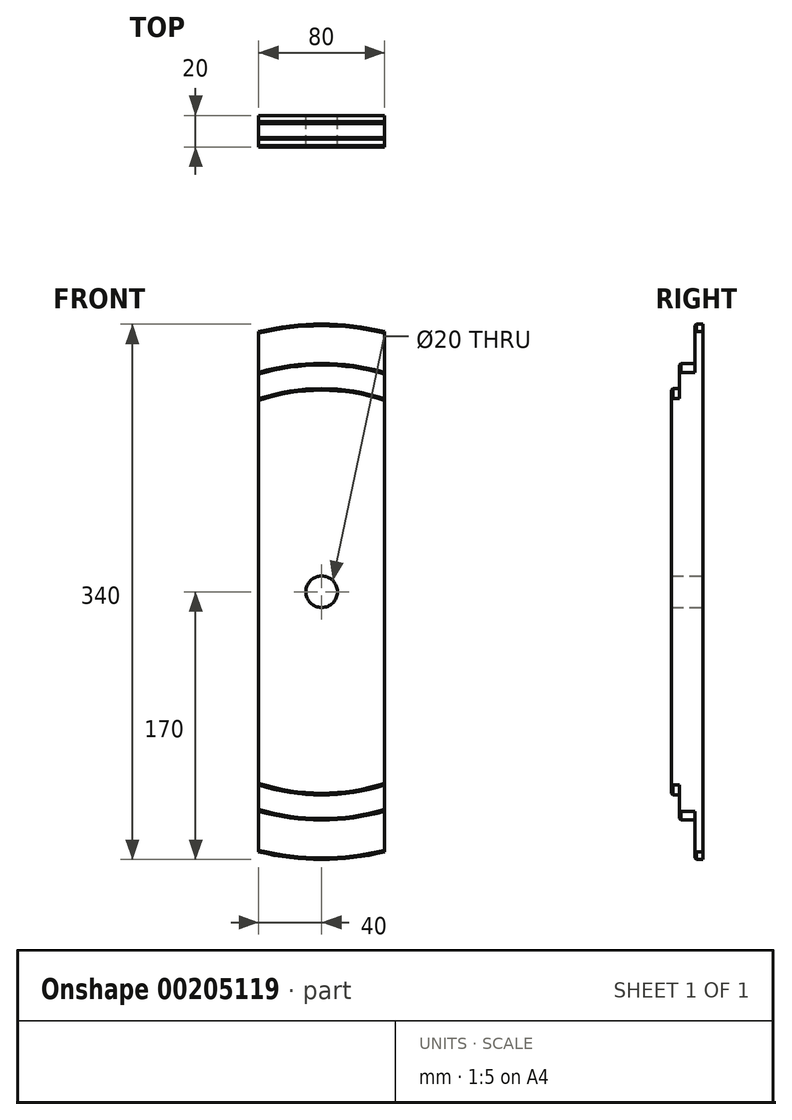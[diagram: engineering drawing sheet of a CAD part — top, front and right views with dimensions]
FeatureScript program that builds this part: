
annotation { "Feature Type Name" : "Feature", "Feature Type Description" : "" }
export const myFeature = defineFeature(function(context is Context, id is Id, definition is map)
    precondition{}
    {
        {
            var Q0;
            Q0=qCreatedBy(makeId("Front.planeOp"),FACE);
            var sketch = newSketch(context, id + "F0", { "sketchPlane" : qUnion([Q0])});
            skCircle(sketch, "E0", {"center": v(0, 0) * mm, "radius": 170 * mm});
            skCircle(sketch, "E1", {"center": v(0, 0) * mm, "radius": 145 * mm});
            skCircle(sketch, "E2", {"center": v(0, 0) * mm, "radius": 129 * mm});
            skLineSegment(sketch, "E3.bottom", {"start": v(-40, 175.47) * mm, "end": v(40, 175.47) * mm});
            skLineSegment(sketch, "E3.top", {"start": v(-40, -184.43) * mm, "end": v(40, -184.43) * mm});
            skLineSegment(sketch, "E3.left", {"start": v(-40, 175.47) * mm, "end": v(-40, -184.43) * mm});
            skLineSegment(sketch, "E3.right", {"start": v(40, 175.47) * mm, "end": v(40, -184.43) * mm});
            skCircle(sketch, "E4", {"center": v(0, 0) * mm, "radius": 10 * mm});
            skSolve(sketch);
        }
        {
            var Q0;
            Q0=makeQuery(id+"F0.imprint","IMPRINT",FACE,{"disambiguationData":[TD([[makeQuery(id+"F0.imprint","IMPRINT",EDGE,{"derivedFrom":sQuery(id+"F0.wireOp",EDGE,"E0")}),1.0]])]});
            extrude(context, id + "F1", {"entities" : qUnion([Q0]), "depth" : 5 * mm});
        }
        {
            var Q0;
            Q0=makeQuery(id+"F0.imprint","IMPRINT",FACE,{"disambiguationData":[TD([[makeQuery(id+"F0.imprint","IMPRINT",EDGE,{"derivedFrom":sQuery(id+"F0.wireOp",EDGE,"E1")}),1.0]])]});
            extrude(context, id + "F2", {"entities" : qUnion([Q0]), "operationType" : NewBodyOperationType.ADD, "depth" : 15 * mm});
        }
        {
            var Q0;
            Q0=makeQuery(id+"F0.imprint","IMPRINT",FACE,{"disambiguationData":[TD([[makeQuery(id+"F0.imprint","IMPRINT",EDGE,{"derivedFrom":sQuery(id+"F0.wireOp",EDGE,"E2")}),1.0]])]});
            extrude(context, id + "F3", {"entities" : qUnion([Q0]), "operationType" : NewBodyOperationType.ADD, "depth" : 20 * mm});
        }
        {
            var Q0;
            {var subQ0=sQuery(id+"F0.wireOp",EDGE,"E3.left");var subQ1=sQuery(id+"F0.wireOp",EDGE,"E2");var subQ2=makeQuery(id+"F0.imprint","INTERSECT",VERTEX,{"disambiguationData":[OD(0.0)],"derivedFrom":[subQ1,subQ0]});Q0=makeQuery(id+"F0.imprint","IMPRINT",FACE,{"disambiguationData":[TD([[makeQuery(id+"F0.imprint","IMPRINT",EDGE,{"disambiguationData":[TD([[subQ2,-1.0]])],"derivedFrom":subQ1}),1.0]])]});}
            var Q1;
            {var subQ0=sQuery(id+"F0.wireOp",EDGE,"E3.left");var subQ1=sQuery(id+"F0.wireOp",EDGE,"E1");var subQ2=makeQuery(id+"F0.imprint","INTERSECT",VERTEX,{"disambiguationData":[OD(0.0)],"derivedFrom":[subQ1,subQ0]});Q1=makeQuery(id+"F0.imprint","IMPRINT",FACE,{"disambiguationData":[TD([[makeQuery(id+"F0.imprint","IMPRINT",EDGE,{"disambiguationData":[TD([[subQ2,-1.0]])],"derivedFrom":subQ1}),1.0]])]});}
            var Q2;
            {var subQ0=sQuery(id+"F0.wireOp",EDGE,"E3.left");var subQ1=sQuery(id+"F0.wireOp",EDGE,"E0");var subQ2=makeQuery(id+"F0.imprint","INTERSECT",VERTEX,{"disambiguationData":[OD(0.0)],"derivedFrom":[subQ1,subQ0]});Q2=makeQuery(id+"F0.imprint","IMPRINT",FACE,{"disambiguationData":[TD([[makeQuery(id+"F0.imprint","IMPRINT",EDGE,{"disambiguationData":[TD([[subQ2,-1.0]])],"derivedFrom":subQ1}),1.0]])]});}
            var Q3;
            {var subQ0=sQuery(id+"F0.wireOp",EDGE,"E3.right");var subQ1=sQuery(id+"F0.wireOp",EDGE,"E0");var subQ2=makeQuery(id+"F0.imprint","INTERSECT",VERTEX,{"disambiguationData":[OD(0.0)],"derivedFrom":[subQ1,subQ0]});Q3=makeQuery(id+"F0.imprint","IMPRINT",FACE,{"disambiguationData":[TD([[makeQuery(id+"F0.imprint","IMPRINT",EDGE,{"disambiguationData":[TD([[subQ2,1.0]])],"derivedFrom":subQ1}),1.0]])]});}
            var Q4;
            {var subQ0=sQuery(id+"F0.wireOp",EDGE,"E3.right");var subQ1=sQuery(id+"F0.wireOp",EDGE,"E1");var subQ2=makeQuery(id+"F0.imprint","INTERSECT",VERTEX,{"disambiguationData":[OD(0.0)],"derivedFrom":[subQ1,subQ0]});Q4=makeQuery(id+"F0.imprint","IMPRINT",FACE,{"disambiguationData":[TD([[makeQuery(id+"F0.imprint","IMPRINT",EDGE,{"disambiguationData":[TD([[subQ2,1.0]])],"derivedFrom":subQ1}),1.0]])]});}
            var Q5;
            {var subQ0=sQuery(id+"F0.wireOp",EDGE,"E3.right");var subQ1=sQuery(id+"F0.wireOp",EDGE,"E2");var subQ2=makeQuery(id+"F0.imprint","INTERSECT",VERTEX,{"disambiguationData":[OD(0.0)],"derivedFrom":[subQ1,subQ0]});Q5=makeQuery(id+"F0.imprint","IMPRINT",FACE,{"disambiguationData":[TD([[makeQuery(id+"F0.imprint","IMPRINT",EDGE,{"disambiguationData":[TD([[subQ2,1.0]])],"derivedFrom":subQ1}),1.0]])]});}
            extrude(context, id + "F4", {"entities" : qUnion([Q0, Q1, Q2, Q3, Q4, Q5]), "operationType" : NewBodyOperationType.REMOVE, "depth" : 30 * mm});
        }
        {
            var Q0;
            {var subQ0=sQuery(id+"F0.wireOp",EDGE,"E2");Q0=makeQuery(id+"F3.opExtrude","CAP_EDGE",EDGE,{"disambiguationData":[OSD([subQ0]),TDD([makeQuery(id+"F0.imprint","IMPRINT",EDGE,{"disambiguationData":[TD([[makeQuery(id+"F0.imprint","INTERSECT",VERTEX,{"disambiguationData":[OD(0.0)],"derivedFrom":[subQ0,sQuery(id+"F0.wireOp",EDGE,"E3.left")]}),1.0]])],"derivedFrom":subQ0})])],"isStart":false});}
            var Q1;
            Q1=makeQuery(id+"F4.boolean.opBoolean","SPLIT",EDGE,{"disambiguationData":[OD(0.0)],"derivedFrom":makeQuery(id+"F2.opExtrude","CAP_EDGE",EDGE,{"disambiguationData":[OSD([sQuery(id+"F0.wireOp",EDGE,"E1")])],"isStart":false})});
            var Q2;
            Q2=makeQuery(id+"F4.boolean.opBoolean","SPLIT",EDGE,{"disambiguationData":[OD(0.0)],"derivedFrom":makeQuery(id+"F1.opExtrude","CAP_EDGE",EDGE,{"disambiguationData":[OSD([sQuery(id+"F0.wireOp",EDGE,"E0")])],"isStart":false})});
            var Q3;
            {var subQ0=sQuery(id+"F0.wireOp",EDGE,"E2");Q3=makeQuery(id+"F3.opExtrude","CAP_EDGE",EDGE,{"disambiguationData":[OSD([subQ0]),TDD([makeQuery(id+"F0.imprint","IMPRINT",EDGE,{"disambiguationData":[TD([[makeQuery(id+"F0.imprint","INTERSECT",VERTEX,{"disambiguationData":[OD(1.0)],"derivedFrom":[subQ0,sQuery(id+"F0.wireOp",EDGE,"E3.left")]}),-1.0]])],"derivedFrom":subQ0})])],"isStart":false});}
            var Q4;
            Q4=makeQuery(id+"F4.boolean.opBoolean","SPLIT",EDGE,{"disambiguationData":[OD(1.0)],"derivedFrom":makeQuery(id+"F2.opExtrude","CAP_EDGE",EDGE,{"disambiguationData":[OSD([sQuery(id+"F0.wireOp",EDGE,"E1")])],"isStart":false})});
            var Q5;
            Q5=makeQuery(id+"F4.boolean.opBoolean","SPLIT",EDGE,{"disambiguationData":[OD(1.0)],"derivedFrom":makeQuery(id+"F1.opExtrude","CAP_EDGE",EDGE,{"disambiguationData":[OSD([sQuery(id+"F0.wireOp",EDGE,"E0")])],"isStart":false})});
            chamfer(context, id + "F5", {"entities" : qUnion([Q0, Q1, Q2, Q3, Q4, Q5]), "width" : 1 * mm, "tangentPropagation" : true});
        }
    });
